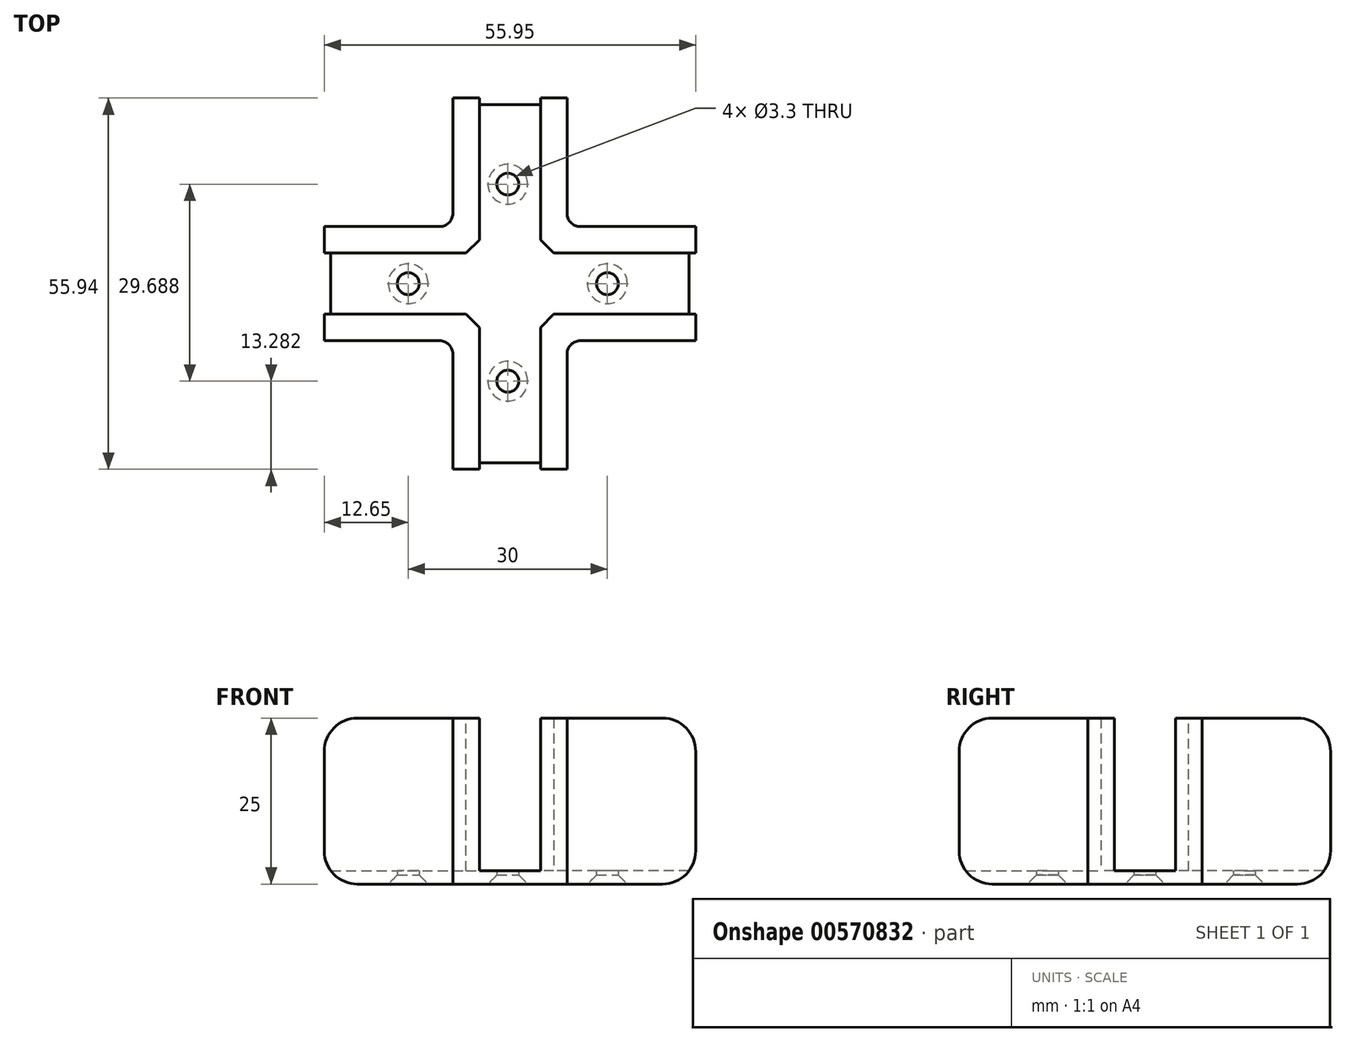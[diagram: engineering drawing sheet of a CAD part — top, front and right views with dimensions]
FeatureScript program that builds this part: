
annotation { "Feature Type Name" : "Feature", "Feature Type Description" : "" }
export const myFeature = defineFeature(function(context is Context, id is Id, definition is map)
    precondition{}
    {
        {
            var Q0;
            Q0=qCreatedBy(makeId("Top.planeOp"),FACE);
            var sketch = newSketch(context, id + "F0", { "sketchPlane" : qUnion([Q0])});
            skLineSegment(sketch, "E0", {"start": v(28.3, 9.2) * mm, "end": v(4.92, 9.2) * mm});
            skLineSegment(sketch, "E1", {"start": v(4.92, 9.2) * mm, "end": v(4.92, 32.57) * mm});
            skLineSegment(sketch, "E2", {"start": v(-4.28, 32.57) * mm, "end": v(-4.28, 9.2) * mm});
            skLineSegment(sketch, "E3", {"start": v(-4.28, 9.2) * mm, "end": v(-27.65, 9.2) * mm});
            skLineSegment(sketch, "E4.0", {"start": v(8.92, 32.57) * mm, "end": v(-8.28, 32.57) * mm});
            skLineSegment(sketch, "E4.1", {"start": v(8.92, 13.2) * mm, "end": v(8.92, 32.57) * mm});
            skLineSegment(sketch, "E4.2", {"start": v(-8.28, 32.57) * mm, "end": v(-8.28, 13.2) * mm});
            skLineSegment(sketch, "E4.3", {"start": v(28.3, 13.2) * mm, "end": v(8.92, 13.2) * mm});
            skLineSegment(sketch, "E4.4", {"start": v(28.3, -4) * mm, "end": v(28.3, 13.2) * mm});
            skLineSegment(sketch, "E4.5", {"start": v(-8.28, 13.2) * mm, "end": v(-27.65, 13.2) * mm});
            skLineSegment(sketch, "E4.6", {"start": v(-27.65, 13.2) * mm, "end": v(-27.65, -4) * mm});
            skLineSegment(sketch, "E5", {"start": v(-27.65, 0) * mm, "end": v(-4.28, 0) * mm});
            skLineSegment(sketch, "E6", {"start": v(-4.28, 0) * mm, "end": v(-4.28, -23.37) * mm});
            skLineSegment(sketch, "E7", {"start": v(4.92, -23.37) * mm, "end": v(4.92, 0) * mm});
            skLineSegment(sketch, "E8", {"start": v(4.92, 0) * mm, "end": v(28.3, 0) * mm});
            skLineSegment(sketch, "E9.0", {"start": v(8.92, -4) * mm, "end": v(28.3, -4) * mm});
            skLineSegment(sketch, "E9.1", {"start": v(-27.65, -4) * mm, "end": v(-8.28, -4) * mm});
            skLineSegment(sketch, "E9.2", {"start": v(-8.28, -4) * mm, "end": v(-8.28, -23.37) * mm});
            skLineSegment(sketch, "E9.3", {"start": v(-8.28, -23.37) * mm, "end": v(8.92, -23.37) * mm});
            skLineSegment(sketch, "E9.4", {"start": v(8.92, -23.37) * mm, "end": v(8.92, -4) * mm});
            skSolve(sketch);
        }
        {
            var Q0;
            Q0=qSketchRegion(id+"F0",true);
            extrude(context, id + "F1", {"entities" : qUnion([Q0]), "depth" : 2 * mm, "offsetDistance" : 25 * mm});
        }
        {
            var Q0;
            {var subQ1=sQuery(id+"F0.wireOp",EDGE,"E2");Q0=makeQuery(id+"F0.imprint","IMPRINT",FACE,{"disambiguationData":[TD([[makeQuery(id+"F0.imprint","IMPRINT",EDGE,{"derivedFrom":subQ1}),-1.0]])]});}
            var Q1;
            {var subQ4=sQuery(id+"F0.wireOp",EDGE,"E0");Q1=makeQuery(id+"F0.imprint","IMPRINT",FACE,{"disambiguationData":[TD([[makeQuery(id+"F0.imprint","IMPRINT",EDGE,{"derivedFrom":subQ4}),-1.0]])]});}
            var Q2;
            {var subQ2=sQuery(id+"F0.wireOp",EDGE,"E5");Q2=makeQuery(id+"F0.imprint","IMPRINT",FACE,{"disambiguationData":[TD([[makeQuery(id+"F0.imprint","IMPRINT",EDGE,{"derivedFrom":subQ2}),-1.0]])]});}
            var Q3;
            {var subQ3=sQuery(id+"F0.wireOp",EDGE,"E7");Q3=makeQuery(id+"F0.imprint","IMPRINT",FACE,{"disambiguationData":[TD([[makeQuery(id+"F0.imprint","IMPRINT",EDGE,{"derivedFrom":subQ3}),-1.0]])]});}
            extrude(context, id + "F2", {"entities" : qUnion([Q0, Q1, Q2, Q3]), "operationType" : NewBodyOperationType.ADD, "depth" : 25 * mm, "offsetDistance" : 25 * mm});
        }
        {
            var Q0;
            {var subQ0=sQuery(id+"F0.wireOp",EDGE,"E4.3");var subQ1=sQuery(id+"F0.wireOp",EDGE,"E4.1");Q0=makeQuery(id+"F2.boolean.opBoolean","MERGE",EDGE,{"derivedFrom":[makeQuery(id+"F1.opExtrude","SWEPT_EDGE",EDGE,{"disambiguationData":[OSD([subQ1,subQ0])]}),makeQuery(id+"F2.opExtrude","SWEPT_EDGE",EDGE,{"disambiguationData":[OSD([subQ1,subQ0])]})]});}
            var Q1;
            {var subQ0=sQuery(id+"F0.wireOp",EDGE,"E9.4");var subQ1=sQuery(id+"F0.wireOp",EDGE,"E9.0");Q1=makeQuery(id+"F2.boolean.opBoolean","MERGE",EDGE,{"derivedFrom":[makeQuery(id+"F1.opExtrude","SWEPT_EDGE",EDGE,{"disambiguationData":[OSD([subQ1,subQ0])]}),makeQuery(id+"F2.opExtrude","SWEPT_EDGE",EDGE,{"disambiguationData":[OSD([subQ1,subQ0])]})]});}
            fillet(context, id + "F3", {"entities" : qUnion([Q0, Q1]), "radius" : 2 * mm, "tangentPropagation" : true, "allowEdgeOverflow" : false});
        }
        {
            var Q0;
            {var subQ0=sQuery(id+"F0.wireOp",EDGE,"E4.4");Q0=makeQuery(id+"F2.opExtrude","CAP_EDGE",EDGE,{"disambiguationData":[OSD([subQ0]),TDD([makeQuery(id+"F0.imprint","IMPRINT",EDGE,{"disambiguationData":[TD([[makeQuery(id+"F0.imprint","INTERSECT",VERTEX,{"derivedFrom":[sQuery(id+"F0.wireOp",EDGE,"4AKFVKuP-VGzW-Z0gR-biP7-avwRZvC0l9sY"),subQ0]}),1.0]])],"derivedFrom":subQ0})])],"isStart":false});}
            var Q1;
            {var subQ0=sQuery(id+"F0.wireOp",EDGE,"E4.4");Q1=makeQuery(id+"F2.opExtrude","CAP_EDGE",EDGE,{"disambiguationData":[OSD([subQ0]),TDD([makeQuery(id+"F0.imprint","IMPRINT",EDGE,{"disambiguationData":[TD([[makeQuery(id+"F0.imprint","INTERSECT",VERTEX,{"derivedFrom":[sQuery(id+"F0.wireOp",EDGE,"E0"),subQ0]}),-1.0]])],"derivedFrom":subQ0})])],"isStart":false});}
            var Q2;
            {var subQ0=sQuery(id+"F0.wireOp",EDGE,"E4.6");Q2=makeQuery(id+"F2.opExtrude","CAP_EDGE",EDGE,{"disambiguationData":[OSD([subQ0]),TDD([makeQuery(id+"F0.imprint","IMPRINT",EDGE,{"disambiguationData":[TD([[makeQuery(id+"F0.imprint","INTERSECT",VERTEX,{"derivedFrom":[sQuery(id+"F0.wireOp",EDGE,"34O9V31c-Diq1-Ufnw-3ykA-mJ2vG209VLsY"),subQ0]}),-1.0]])],"derivedFrom":subQ0})])],"isStart":false});}
            var Q3;
            {var subQ0=sQuery(id+"F0.wireOp",EDGE,"E4.6");Q3=makeQuery(id+"F2.opExtrude","CAP_EDGE",EDGE,{"disambiguationData":[OSD([subQ0]),TDD([makeQuery(id+"F0.imprint","IMPRINT",EDGE,{"disambiguationData":[TD([[makeQuery(id+"F0.imprint","INTERSECT",VERTEX,{"derivedFrom":[sQuery(id+"F0.wireOp",EDGE,"E3"),subQ0]}),1.0]])],"derivedFrom":subQ0})])],"isStart":false});}
            var Q4;
            {var subQ0=sQuery(id+"F0.wireOp",EDGE,"E4.0");Q4=makeQuery(id+"F2.opExtrude","CAP_EDGE",EDGE,{"disambiguationData":[OSD([subQ0]),TDD([makeQuery(id+"F0.imprint","IMPRINT",EDGE,{"disambiguationData":[TD([[makeQuery(id+"F0.imprint","INTERSECT",VERTEX,{"derivedFrom":[sQuery(id+"F0.wireOp",EDGE,"E2"),subQ0]}),-1.0]])],"derivedFrom":subQ0})])],"isStart":false});}
            var Q5;
            {var subQ0=sQuery(id+"F0.wireOp",EDGE,"E4.0");Q5=makeQuery(id+"F2.opExtrude","CAP_EDGE",EDGE,{"disambiguationData":[OSD([subQ0]),TDD([makeQuery(id+"F0.imprint","IMPRINT",EDGE,{"disambiguationData":[TD([[makeQuery(id+"F0.imprint","INTERSECT",VERTEX,{"derivedFrom":[sQuery(id+"F0.wireOp",EDGE,"E1"),subQ0]}),1.0]])],"derivedFrom":subQ0})])],"isStart":false});}
            var Q6;
            Q6=makeQuery(id+"F1.opExtrude","CAP_EDGE",EDGE,{"disambiguationData":[OSD([sQuery(id+"F0.wireOp",EDGE,"E4.6")])],"isStart":true});
            var Q7;
            Q7=makeQuery(id+"F1.opExtrude","CAP_EDGE",EDGE,{"disambiguationData":[OSD([sQuery(id+"F0.wireOp",EDGE,"E4.4")])],"isStart":true});
            var Q8;
            Q8=makeQuery(id+"F1.opExtrude","CAP_EDGE",EDGE,{"disambiguationData":[OSD([sQuery(id+"F0.wireOp",EDGE,"E4.0")])],"isStart":true});
            var Q9;
            Q9=makeQuery(id+"F1.opExtrude","CAP_EDGE",EDGE,{"disambiguationData":[OSD([sQuery(id+"F0.wireOp",EDGE,"E9.3")])],"isStart":true});
            var Q10;
            {var subQ0=sQuery(id+"F0.wireOp",EDGE,"E9.3");Q10=makeQuery(id+"F2.opExtrude","CAP_EDGE",EDGE,{"disambiguationData":[OSD([subQ0]),TDD([makeQuery(id+"F0.imprint","IMPRINT",EDGE,{"disambiguationData":[TD([[makeQuery(id+"F0.imprint","INTERSECT",VERTEX,{"derivedFrom":[sQuery(id+"F0.wireOp",EDGE,"E6"),subQ0]}),1.0]])],"derivedFrom":subQ0})])],"isStart":false});}
            var Q11;
            {var subQ0=sQuery(id+"F0.wireOp",EDGE,"E9.3");Q11=makeQuery(id+"F2.opExtrude","CAP_EDGE",EDGE,{"disambiguationData":[OSD([subQ0]),TDD([makeQuery(id+"F0.imprint","IMPRINT",EDGE,{"disambiguationData":[TD([[makeQuery(id+"F0.imprint","INTERSECT",VERTEX,{"derivedFrom":[sQuery(id+"F0.wireOp",EDGE,"E7"),subQ0]}),-1.0]])],"derivedFrom":subQ0})])],"isStart":false});}
            fillet(context, id + "F4", {"entities" : qUnion([Q0, Q1, Q2, Q3, Q4, Q5, Q6, Q7, Q8, Q9, Q10, Q11]), "radius" : 5 * mm, "tangentPropagation" : true, "allowEdgeOverflow" : false});
        }
        {
            var Q0;
            {var subQ0=sQuery(id+"F0.wireOp",EDGE,"E4.5");var subQ1=sQuery(id+"F0.wireOp",EDGE,"E4.2");Q0=makeQuery(id+"F2.boolean.opBoolean","MERGE",EDGE,{"derivedFrom":[makeQuery(id+"F1.opExtrude","SWEPT_EDGE",EDGE,{"disambiguationData":[OSD([subQ1,subQ0])]}),makeQuery(id+"F2.opExtrude","SWEPT_EDGE",EDGE,{"disambiguationData":[OSD([subQ1,subQ0])]})]});}
            var Q1;
            {var subQ0=sQuery(id+"F0.wireOp",EDGE,"E9.2");var subQ1=sQuery(id+"F0.wireOp",EDGE,"E9.1");Q1=makeQuery(id+"F2.boolean.opBoolean","MERGE",EDGE,{"derivedFrom":[makeQuery(id+"F1.opExtrude","SWEPT_EDGE",EDGE,{"disambiguationData":[OSD([subQ1,subQ0])]}),makeQuery(id+"F2.opExtrude","SWEPT_EDGE",EDGE,{"disambiguationData":[OSD([subQ1,subQ0])]})]});}
            fillet(context, id + "F5", {"entities" : qUnion([Q0, Q1]), "radius" : 2 * mm, "tangentPropagation" : true, "allowEdgeOverflow" : false});
        }
        {
            var Q0;
            Q0=makeQuery(id+"F2.opExtrude","SWEPT_EDGE",EDGE,{"disambiguationData":[OSD([sQuery(id+"F0.wireOp",EDGE,"E0"),sQuery(id+"F0.wireOp",EDGE,"E1")])]});
            var Q1;
            Q1=makeQuery(id+"F2.opExtrude","SWEPT_EDGE",EDGE,{"disambiguationData":[OSD([sQuery(id+"F0.wireOp",EDGE,"E2"),sQuery(id+"F0.wireOp",EDGE,"E3")])]});
            var Q2;
            Q2=makeQuery(id+"F2.opExtrude","SWEPT_EDGE",EDGE,{"disambiguationData":[OSD([sQuery(id+"F0.wireOp",EDGE,"E7"),sQuery(id+"F0.wireOp",EDGE,"E8")])]});
            var Q3;
            Q3=makeQuery(id+"F2.opExtrude","SWEPT_EDGE",EDGE,{"disambiguationData":[OSD([sQuery(id+"F0.wireOp",EDGE,"E5"),sQuery(id+"F0.wireOp",EDGE,"E6")])]});
            chamfer(context, id + "F6", {"entities" : qUnion([Q0, Q1, Q2, Q3]), "width" : 2 * mm, "tangentPropagation" : true});
        }
        {
            var Q0;
            {var subQ9=sQuery(id+"F0.wireOp",EDGE,"E0");Q0=makeQuery(id+"F0.imprint","IMPRINT",FACE,{"disambiguationData":[TD([[makeQuery(id+"F0.imprint","IMPRINT",EDGE,{"derivedFrom":subQ9}),1.0]])]});}
            var sketch = newSketch(context, id + "F7", { "sketchPlane" : qUnion([Q0])});
            skLineSegment(sketch, "E10", {"start": v(0, -18.75) * mm, "end": v(0, 32.62) * mm});
            skLineSegment(sketch, "E11", {"start": v(-27.5, 4.6) * mm, "end": v(28.43, 4.6) * mm});
            skPoint(sketch, "E12", {"position": v(-15, 4.6) * mm});
            skPoint(sketch, "E13", {"position": v(15, 4.6) * mm});
            skPoint(sketch, "E14", {"position": v(0, -10.09) * mm});
            skPoint(sketch, "E15", {"position": v(0, 19.6) * mm});
            skSolve(sketch);
        }
        {
            var Q0;
            Q0=sQuery(id+"F7.wireOp",VERTEX,"E14");
            var Q1;
            Q1=sQuery(id+"F7.wireOp",VERTEX,"E12");
            var Q2;
            Q2=sQuery(id+"F7.wireOp",VERTEX,"E13");
            var Q3;
            Q3=sQuery(id+"F7.wireOp",VERTEX,"E15");
            var Q4;
            Q4=makeQuery(id+"F1.opExtrude","SWEPT_BODY",BODY,{"disambiguationData":[OSD([sQuery(id+"F0.wireOp",EDGE,"E4.0"),sQuery(id+"F0.wireOp",EDGE,"E4.1"),sQuery(id+"F0.wireOp",EDGE,"E4.2"),sQuery(id+"F0.wireOp",EDGE,"E4.3"),sQuery(id+"F0.wireOp",EDGE,"E4.4"),sQuery(id+"F0.wireOp",EDGE,"E4.5"),sQuery(id+"F0.wireOp",EDGE,"E4.6"),sQuery(id+"F0.wireOp",EDGE,"E9.0"),sQuery(id+"F0.wireOp",EDGE,"E9.1"),sQuery(id+"F0.wireOp",EDGE,"E9.2"),sQuery(id+"F0.wireOp",EDGE,"E9.3"),sQuery(id+"F0.wireOp",EDGE,"E9.4")])]});
            hole(context, id + "F8", {"style" : HoleStyle.C_SINK, "endStyle" : HoleEndStyle.THROUGH, "oppositeDirection" : true, "holeDiameter" : 3.3 * mm, "cSinkDiameter" : 6 * mm, "cSinkAngle" : 90 * degree, "majorDiameter" : 3 * mm, "isTappedThrough" : true, "tappedDepth" : 12 * mm, "tapClearance" : 3, "locations" : qUnion([Q0, Q1, Q2, Q3]), "scope" : qUnion([Q4])});
        }
    });
